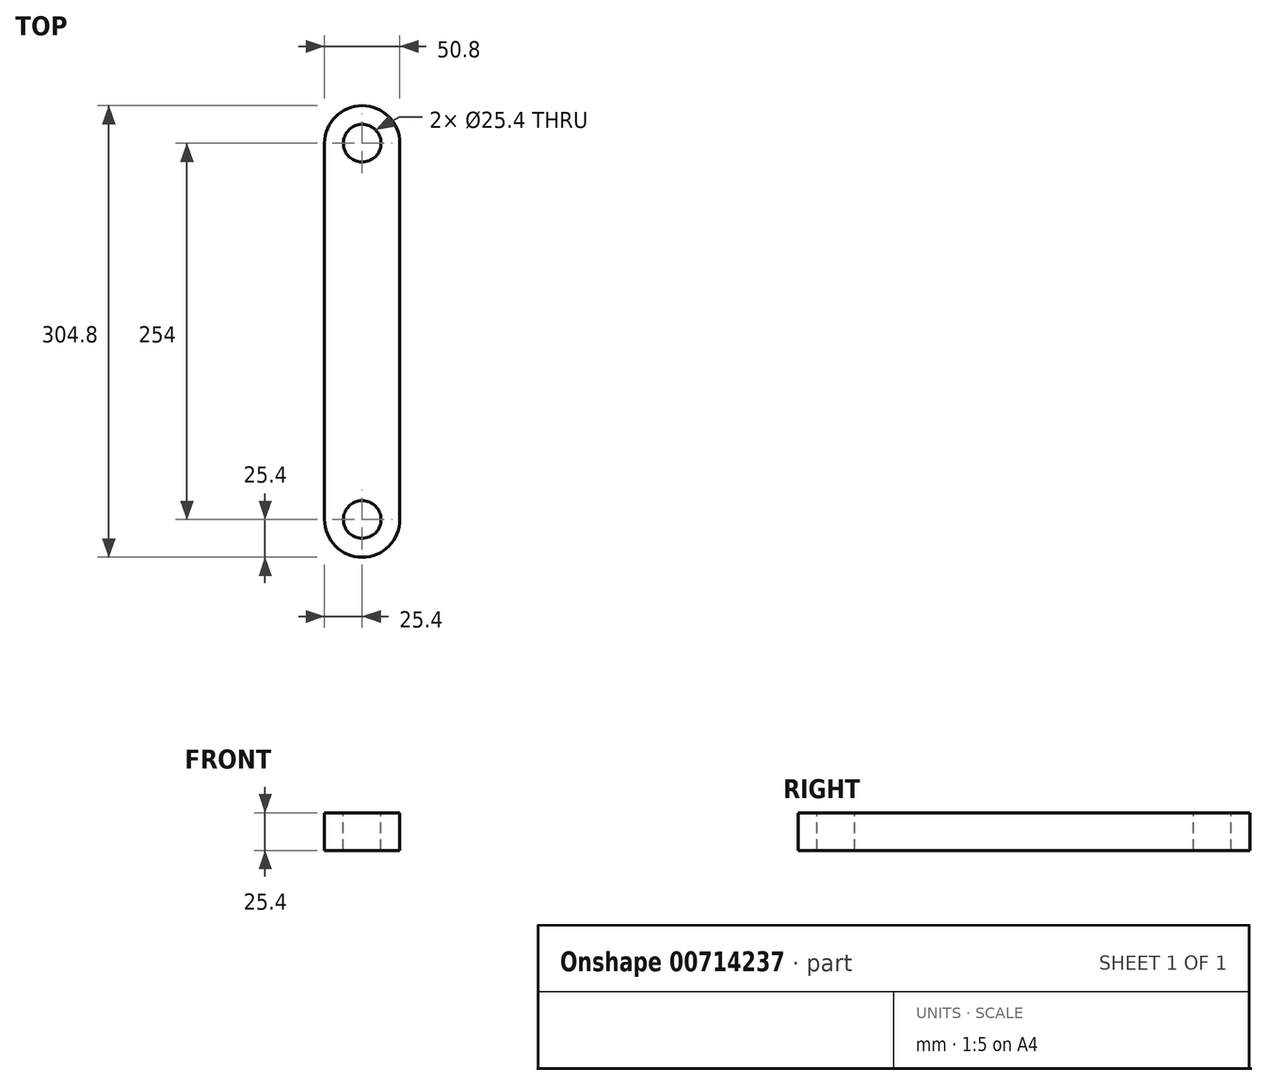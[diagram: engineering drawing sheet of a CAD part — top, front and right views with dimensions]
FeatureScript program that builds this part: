
annotation { "Feature Type Name" : "Feature", "Feature Type Description" : "" }
export const myFeature = defineFeature(function(context is Context, id is Id, definition is map)
    precondition{}
    {
        {
            var Q0;
            Q0=qCreatedBy(makeId("Top.planeOp"),FACE);
            var sketch = newSketch(context, id + "F0", { "sketchPlane" : qUnion([Q0])});
            skLineSegment(sketch, "E0.bottom", {"start": v(-25.4, 0) * mm, "end": v(25.4, 0) * mm});
            skLineSegment(sketch, "E0.top", {"start": v(-25.4, 127) * mm, "end": v(25.4, 127) * mm});
            skLineSegment(sketch, "E0.left", {"start": v(-25.4, 0) * mm, "end": v(-25.4, 127) * mm});
            skLineSegment(sketch, "E0.right", {"start": v(25.4, 0) * mm, "end": v(25.4, 127) * mm});
            skCircle(sketch, "E1", {"center": v(0, 127) * mm, "radius": 25.4 * mm});
            skSolve(sketch);
        }
        {
            var Q0;
            Q0=makeQuery(id+"F0.imprint","IMPRINT",FACE,{"disambiguationData":[TD([[makeQuery(id+"F0.imprint","IMPRINT",EDGE,{"derivedFrom":sQuery(id+"F0.wireOp",EDGE,"E0.bottom")}),1.0]])]});
            var Q1;
            {var subQ0=sQuery(id+"F0.wireOp",EDGE,"E0.top");Q1=makeQuery(id+"F0.imprint","IMPRINT",FACE,{"disambiguationData":[TD([[makeQuery(id+"F0.imprint","IMPRINT",EDGE,{"derivedFrom":subQ0}),1.0]])]});}
            var Q2;
            {var subQ0=sQuery(id+"F0.wireOp",EDGE,"E0.top");Q2=makeQuery(id+"F0.imprint","IMPRINT",FACE,{"disambiguationData":[TD([[makeQuery(id+"F0.imprint","IMPRINT",EDGE,{"derivedFrom":subQ0}),-1.0]])]});}
            extrude(context, id + "F1", {"entities" : qUnion([Q0, Q1, Q2]), "depth" : 25.4 * mm, "offsetDistance" : 25.4 * mm});
        }
        {
            var Q0;
            Q0=makeQuery(id+"F1.opExtrude","CAP_FACE",FACE,{"disambiguationData":[OSD([sQuery(id+"F0.wireOp",EDGE,"E0.bottom"),sQuery(id+"F0.wireOp",EDGE,"E0.left"),sQuery(id+"F0.wireOp",EDGE,"E0.right"),sQuery(id+"F0.wireOp",EDGE,"E1")])],"isStart":false});
            var sketch = newSketch(context, id + "F2", { "sketchPlane" : qUnion([Q0])});
            skCircle(sketch, "E2", {"center": v(0, 127) * mm, "radius": 12.7 * mm});
            skSolve(sketch);
        }
        {
            var Q0;
            Q0=makeQuery(id+"F2.imprint","IMPRINT",FACE,{"disambiguationData":[TD([[makeQuery(id+"F2.imprint","IMPRINT",EDGE,{"derivedFrom":sQuery(id+"F2.wireOp",EDGE,"E2")}),1.0]])]});
            extrude(context, id + "F3", {"entities" : qUnion([Q0]), "operationType" : NewBodyOperationType.REMOVE, "oppositeDirection" : true, "depth" : 25.4 * mm, "offsetDistance" : 25.4 * mm});
        }
        {
            var Q0;
            Q0=makeQuery(id+"F1.opExtrude","SWEPT_BODY",BODY,{"disambiguationData":[OSD([sQuery(id+"F0.wireOp",EDGE,"E0.bottom"),sQuery(id+"F0.wireOp",EDGE,"E0.left"),sQuery(id+"F0.wireOp",EDGE,"E0.right"),sQuery(id+"F0.wireOp",EDGE,"E1")])]});
            var Q1;
            Q1=makeQuery(id+"F1.opExtrude","SWEPT_FACE",FACE,{"disambiguationData":[OSD([sQuery(id+"F0.wireOp",EDGE,"E0.bottom")])]});
            mirror(context, id + "F4", {"operationType" : NewBodyOperationType.ADD, "entities" : qUnion([Q0]), "mirrorPlane" : qUnion([Q1])});
        }
    });
